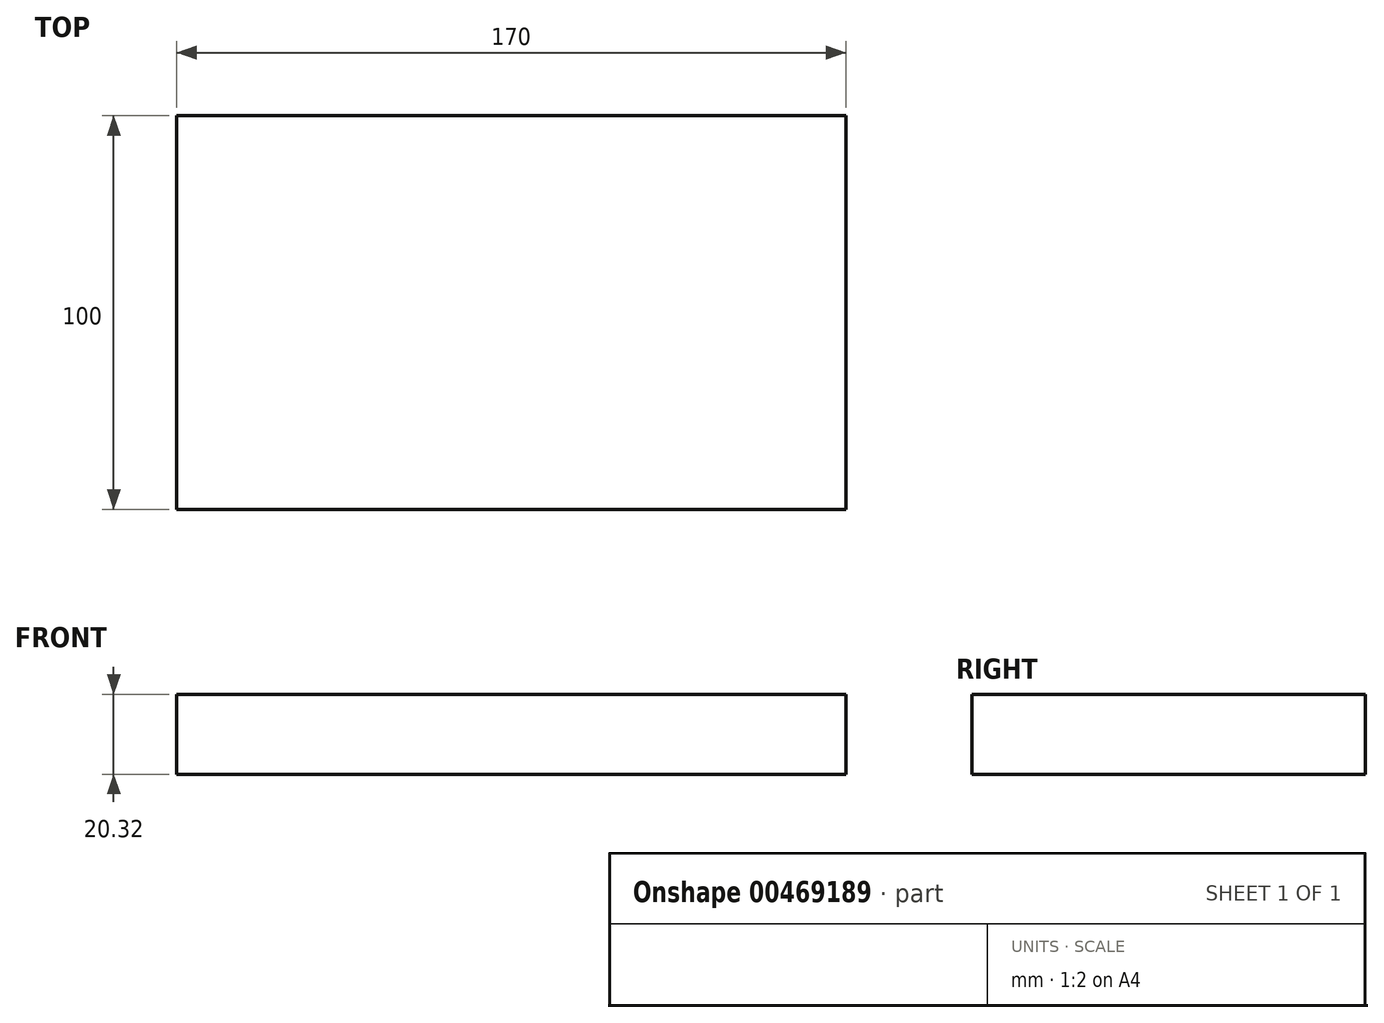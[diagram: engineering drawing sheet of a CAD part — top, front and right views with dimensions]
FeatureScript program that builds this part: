
annotation { "Feature Type Name" : "Feature", "Feature Type Description" : "" }
export const myFeature = defineFeature(function(context is Context, id is Id, definition is map)
    precondition{}
    {
        {
            var Q0;
            Q0=qCreatedBy(makeId("Top.planeOp"),FACE);
            var sketch = newSketch(context, id + "F0", { "sketchPlane" : qUnion([Q0])});
            skLineSegment(sketch, "E0.bottom", {"start": v(85, -50) * mm, "end": v(-85, -50) * mm});
            skLineSegment(sketch, "E0.top", {"start": v(85, 50) * mm, "end": v(-85, 50) * mm});
            skLineSegment(sketch, "E0.left", {"start": v(85, -50) * mm, "end": v(85, 50) * mm});
            skLineSegment(sketch, "E0.right", {"start": v(-85, -50) * mm, "end": v(-85, 50) * mm});
            skPoint(sketch, "E0.middle", {"position": v(0, 0) * mm});
            skSolve(sketch);
        }
        {
            var Q0;
            Q0 = qSketchRegion(id + "F0", true);
            extrude(context, id + "F1", {"entities" : qUnion([Q0]), "depth" : 20.32 * mm});
        }
    });
